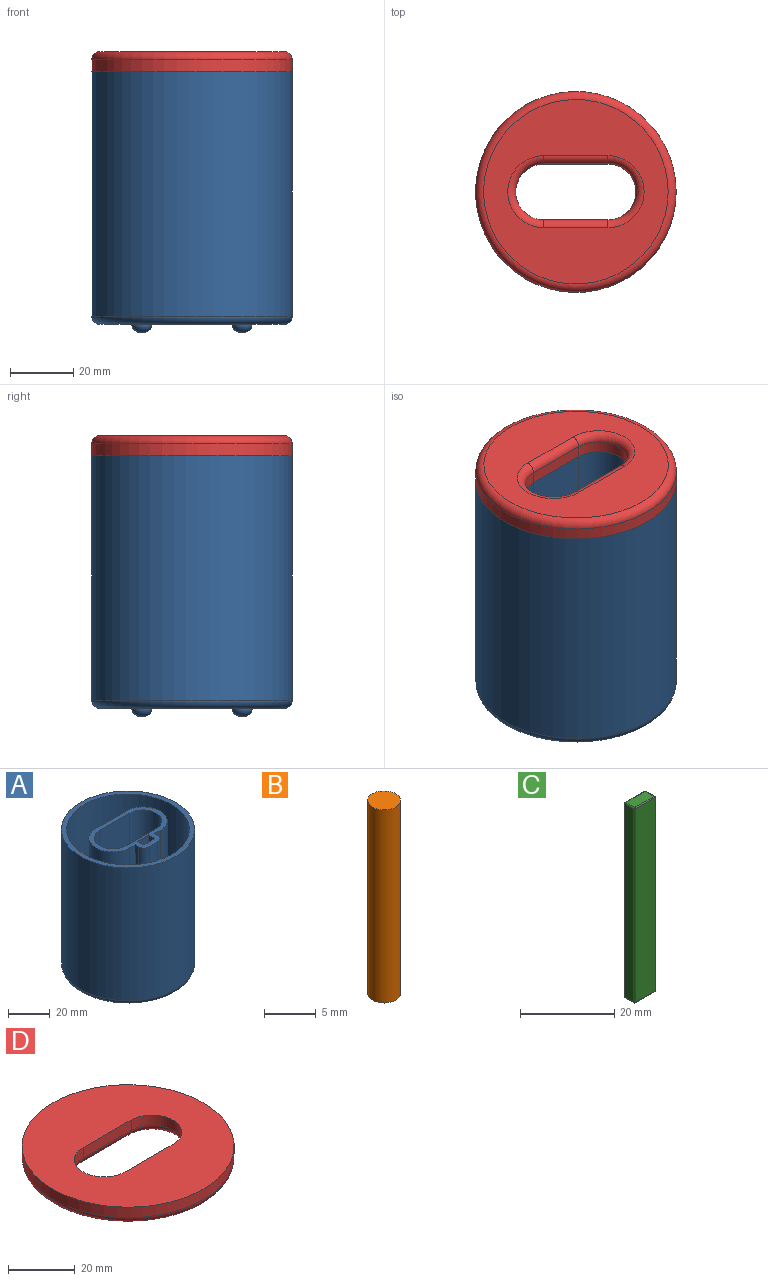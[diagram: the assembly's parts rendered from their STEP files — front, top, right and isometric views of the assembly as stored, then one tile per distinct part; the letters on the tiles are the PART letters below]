
ASSEMBLY  parts=4 mates=3
PART A: 38 faces, bbox 68.7x68.7x82.6 mm
  f0: plane 63.5x63.5mm, normal (0,0,1), area 486.4mm2, adj f5,f28
  f1: plane 77.47x20.32mm, normal (0,-1,0), area 1574.2mm2, adj f2,f4,f6,f34
  f2: cylinder r=8.89mm len=77.47mm, axis (0,0,-1), area 2163.6mm2, adj f1,f3,f6,f33
  f3: plane 77.47x20.32mm, normal (0,1,0), area 1574.2mm2, adj f2,f4,f6,f35
  f4: cylinder r=8.89mm len=77.47mm, axis (0,0,-1), area 2163.6mm2, adj f1,f3,f6,f36
  f5: cylinder r=31.75mm len=77.47mm, axis (0,0,-1), area 15454.6mm2, adj f0,f37
  f6: plane 43.18x28.72mm, normal (0,0,1), area 306.4mm2, adj f1,f2,f3,f4,f8,f9,f10,f11
  f7: plane 58.42x58.42mm, normal (0,0,-1), area 1678.9mm2, adj f17,f18,f19,f20,f33,f34,f35,f36
  f8: plane 73.66x7.37mm, normal (0,-1,0), area 542.6mm2, adj f6,f9,f11,f12
  f9: plane 73.66x4.19mm, normal (1,0,0), area 308.7mm2, adj f6,f8,f10,f12
  f10: plane 73.66x7.37mm, normal (0,1,0), area 542.6mm2, adj f6,f9,f11,f12
  f11: plane 73.66x4.19mm, normal (-1,0,0), area 308.7mm2, adj f6,f8,f10,f12
  f12: plane 7.37x4.19mm, normal (0,0,1), area 30.9mm2, adj f8,f9,f10,f11
  f13: plane 1.27x1.27mm, normal (0,0,-1), area 1.3mm2, adj f17
  f14: plane 1.27x1.27mm, normal (0,0,-1), area 1.3mm2, adj f20
  f15: plane 1.27x1.27mm, normal (0,0,-1), area 1.3mm2, adj f19
  f16: plane 1.27x1.27mm, normal (0,0,-1), area 1.3mm2, adj f18
  f17: torus R=0.64mm, axis (0,0,1), area 56.5mm2, adj f7,f13
  f18: torus R=0.64mm, axis (0,0,1), area 56.5mm2, adj f7,f16
  f19: torus R=0.64mm, axis (0,0,1), area 56.5mm2, adj f7,f15
  f20: torus R=0.64mm, axis (0,0,1), area 56.5mm2, adj f7,f14
  f21: plane 73.66x2.05mm, normal (-1,0,0), area 151.1mm2, adj f6,f22,f30,f32
  f22: plane 73.66x3.47mm, normal (0,-1,0), area 255.3mm2, adj f6,f21,f23,f30
  f23: cylinder r=11.43mm len=73.66mm, axis (0,0,-1), area 2645mm2, adj f6,f22,f24,f30
  f24: plane 73.66x20.32mm, normal (0,1,0), area 1496.8mm2, adj f6,f23,f25,f30
  f25: cylinder r=11.43mm len=73.66mm, axis (0,0,-1), area 2645mm2, adj f6,f24,f26,f30
  f26: plane 73.66x3.52mm, normal (0,-1,0), area 259.3mm2, adj f6,f25,f27,f30
  f27: plane 73.66x2.05mm, normal (1,0,0), area 151.1mm2, adj f6,f26,f30,f31
  f28: cylinder r=29.21mm len=73.66mm, axis (0,0,-1), area 13519mm2, adj f0,f30
  f29: plane 73.66x5.72mm, normal (0,-1,0), area 421mm2, adj f6,f30,f31,f32
  f30: plane 58.42x58.42mm, normal (0,0,1), area 1733.6mm2, adj f21,f22,f23,f24,f25,f26,f27,f28
  f31: cylinder r=3.81mm len=73.66mm, axis (0,0,1), area 440.8mm2, adj f6,f27,f29,f30
  f32: cylinder r=3.81mm len=73.66mm, axis (0,0,-1), area 440.8mm2, adj f6,f21,f29,f30
  f33: torus R=11.43mm, axis (0,0,1), area 123mm2, adj f2,f7,f34,f35
  f34: cylinder r=2.54mm len=20.32mm, axis (1,0,0), area 81.1mm2, adj f1,f7,f33,f36
  f35: cylinder r=2.54mm len=20.32mm, axis (-1,0,0), area 81.1mm2, adj f3,f7,f33,f36
  f36: torus R=11.43mm, axis (0,0,1), area 123mm2, adj f4,f7,f34,f35
  f37: torus R=29.21mm, axis (0,0,1), area 772.8mm2, adj f5,f7
PART B: 3 faces, bbox 3.2x3.2x22.9 mm
  f0: cylinder r=1.59mm len=22.86mm, axis (0,0,-1), area 228mm2, adj f1,f2
  f1: plane 3.18x3.18mm, normal (0,0,1), area 7.9mm2, adj f0
  f2: plane 3.18x3.18mm, normal (0,0,-1), area 7.9mm2, adj f0
PART C: 26 faces, bbox 6.4x3.2x50.8 mm
  f0: plane 50.29x2.67mm, normal (-1,0,0), area 134.1mm2, adj f14,f19,f22,f25
  f1: plane 50.29x5.84mm, normal (0,-1,0), area 293.8mm2, adj f11,f20,f21,f25
  f2: plane 50.29x2.67mm, normal (1,0,0), area 134.1mm2, adj f6,f10,f11,f12
  f3: plane 50.29x5.84mm, normal (0,1,0), area 293.8mm2, adj f6,f9,f13,f14
  f4: plane 5.84x2.67mm, normal (0,0,1), area 15.6mm2, adj f9,f10,f19,f20
  f5: plane 5.84x2.67mm, normal (0,0,-1), area 15.6mm2, adj f12,f13,f21,f22
  f6: cylinder r=0.25mm len=50.29mm, axis (0,0,-1), area 20.1mm2, adj f2,f3,f7,f8
  f7: sphere r=0.25mm, area 0.1mm2, adj f6,f9,f10
  f8: sphere r=0.25mm, area 0.1mm2, adj f6,f12,f13
  f9: cylinder r=0.25mm len=5.84mm, axis (1,0,0), area 2.3mm2, adj f3,f4,f7,f15
  f10: cylinder r=0.25mm len=2.67mm, axis (0,-1,0), area 1.1mm2, adj f2,f4,f7,f16
  f11: cylinder r=0.25mm len=50.29mm, axis (0,0,1), area 20.1mm2, adj f1,f2,f16,f17
  f12: cylinder r=0.25mm len=2.67mm, axis (0,1,0), area 1.1mm2, adj f2,f5,f8,f17
  f13: cylinder r=0.25mm len=5.84mm, axis (-1,0,0), area 2.3mm2, adj f3,f5,f8,f18
  f14: cylinder r=0.25mm len=50.29mm, axis (0,0,1), area 20.1mm2, adj f0,f3,f15,f18
  f15: sphere r=0.25mm, area 0.1mm2, adj f9,f14,f19
  f16: sphere r=0.25mm, area 0.1mm2, adj f10,f11,f20
  f17: sphere r=0.25mm, area 0.1mm2, adj f11,f12,f21
  f18: sphere r=0.25mm, area 0.1mm2, adj f13,f14,f22
  f19: cylinder r=0.25mm len=2.67mm, axis (0,1,0), area 1.1mm2, adj f0,f4,f15,f23
  f20: cylinder r=0.25mm len=5.84mm, axis (-1,0,0), area 2.3mm2, adj f1,f4,f16,f23
  f21: cylinder r=0.25mm len=5.84mm, axis (1,0,0), area 2.3mm2, adj f1,f5,f17,f24
  f22: cylinder r=0.25mm len=2.67mm, axis (0,-1,0), area 1.1mm2, adj f0,f5,f18,f24
  f23: sphere r=0.25mm, area 0.1mm2, adj f19,f20,f25
  f24: sphere r=0.25mm, area 0.1mm2, adj f21,f22,f25
  f25: cylinder r=0.25mm len=50.29mm, axis (0,0,-1), area 20.1mm2, adj f0,f1,f23,f24
PART D: 12 faces, bbox 68.7x68.7x6.4 mm
  f0: plane 20.32x3.81mm, normal (0,-1,0), area 77.4mm2, adj f1,f3,f6,f9
  f1: cylinder r=8.89mm len=17.78mm, axis (0,0,1), area 106.4mm2, adj f0,f2,f6,f10
  f2: plane 20.32x3.81mm, normal (0,1,0), area 77.4mm2, adj f1,f3,f6,f8
  f3: cylinder r=8.89mm len=17.78mm, axis (0,0,1), area 106.4mm2, adj f0,f2,f6,f7
  f4: cylinder r=31.75mm len=63.5mm, axis (0,0,1), area 760.1mm2, adj f6,f11
  f5: plane 58.42x58.42mm, normal (0,0,-1), area 1805.5mm2, adj f7,f8,f9,f10,f11
  f6: plane 63.5x63.5mm, normal (0,0,1), area 2557.3mm2, adj f0,f1,f2,f3,f4
  f7: torus R=11.43mm, axis (0,0,1), area 123mm2, adj f3,f5,f8,f9
  f8: cylinder r=2.54mm len=20.32mm, axis (1,0,0), area 81.1mm2, adj f2,f5,f7,f10
  f9: cylinder r=2.54mm len=20.32mm, axis (-1,0,0), area 81.1mm2, adj f0,f5,f7,f10
  f10: torus R=11.43mm, axis (0,0,1), area 123mm2, adj f1,f5,f8,f9
  f11: torus R=29.21mm, axis (0,0,1), area 772.8mm2, adj f4,f5
PLACE A t=(-57.67,38.2,-18.03)mm
PLACE B t=(18.93,38.64,39.12)mm
PLACE C t=(27.34,-47.53,-11.68)mm
PLACE D rot(axis=(1,0,0),180deg) t=(-57.67,-17.19,61.98)mm
MATE fastened C.f5 <-> A.f12  axis (0,0,-1) through (-19.05,-1.75,-11.68)mm
MATE fastened B.f0 <-> C.f4  axis (0,0,-1) through (-19.05,-1.75,39.12)mm
MATE fastened D.f6 <-> A.f6  axis (0,0,-1) through (-19.05,19.4,61.98)mm
